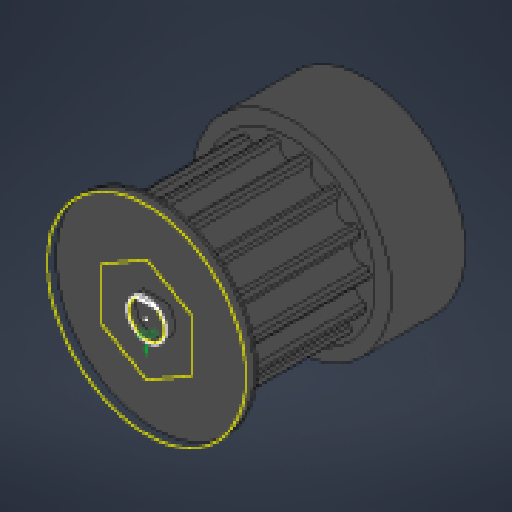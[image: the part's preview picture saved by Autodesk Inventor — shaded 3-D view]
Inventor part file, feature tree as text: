
AUTODESK INVENTOR PART (.ipt)
format: ipt  version: 2024 (Build 280153000, 153)  size: 484,352 bytes
history: native  units: in
note: dims shown in document units (in); Inventor stores cm internally (conversion verified against a paired STEP export)
features: other x6, extrude x4, boolean_combine x1, sketch x1, reference x1
ambient origin geometry x8: Origin, YZ Plane, XZ Plane, XY Plane, X Axis, Y Axis, Z Axis, Center Point
bodies: Solid1 (feature_tree), Solid2 (feature_tree), Solid3 (feature_tree)
feature tree (13):
  boolean_combine  "Combine1"
  sketch  "Sketch1"  dims[d0=0.0098in d1=0.05in d2=0.0in d3=0.05in d4=0.0in d5=0.05in d6=0.0in d7=0.3937in d8=0.0in]
  extrude  "Extrusion1"  Depth=0.3937in TaperAngle=0.0deg
  extrude  "Extrusion2"  Depth=0.3937in TaperAngle=0.0deg
  extrude  "Extrusion3"  Depth=0.3937in TaperAngle=0.0deg
  extrude  "Extrusion4"  Depth=0.3937in TaperAngle=0.0deg
  reference  "Reference1"
  other  "Cut-Revolve1[2]"
  other  "Cut-Extrude4"
  other  "Cut-Extrude5"
  other  "<userpath>\CodingProjects\C-AAM\CAD\V1\Base.iam"
  other  "Base.iam"
  other  "6627T91_Stepper Motor:1"
